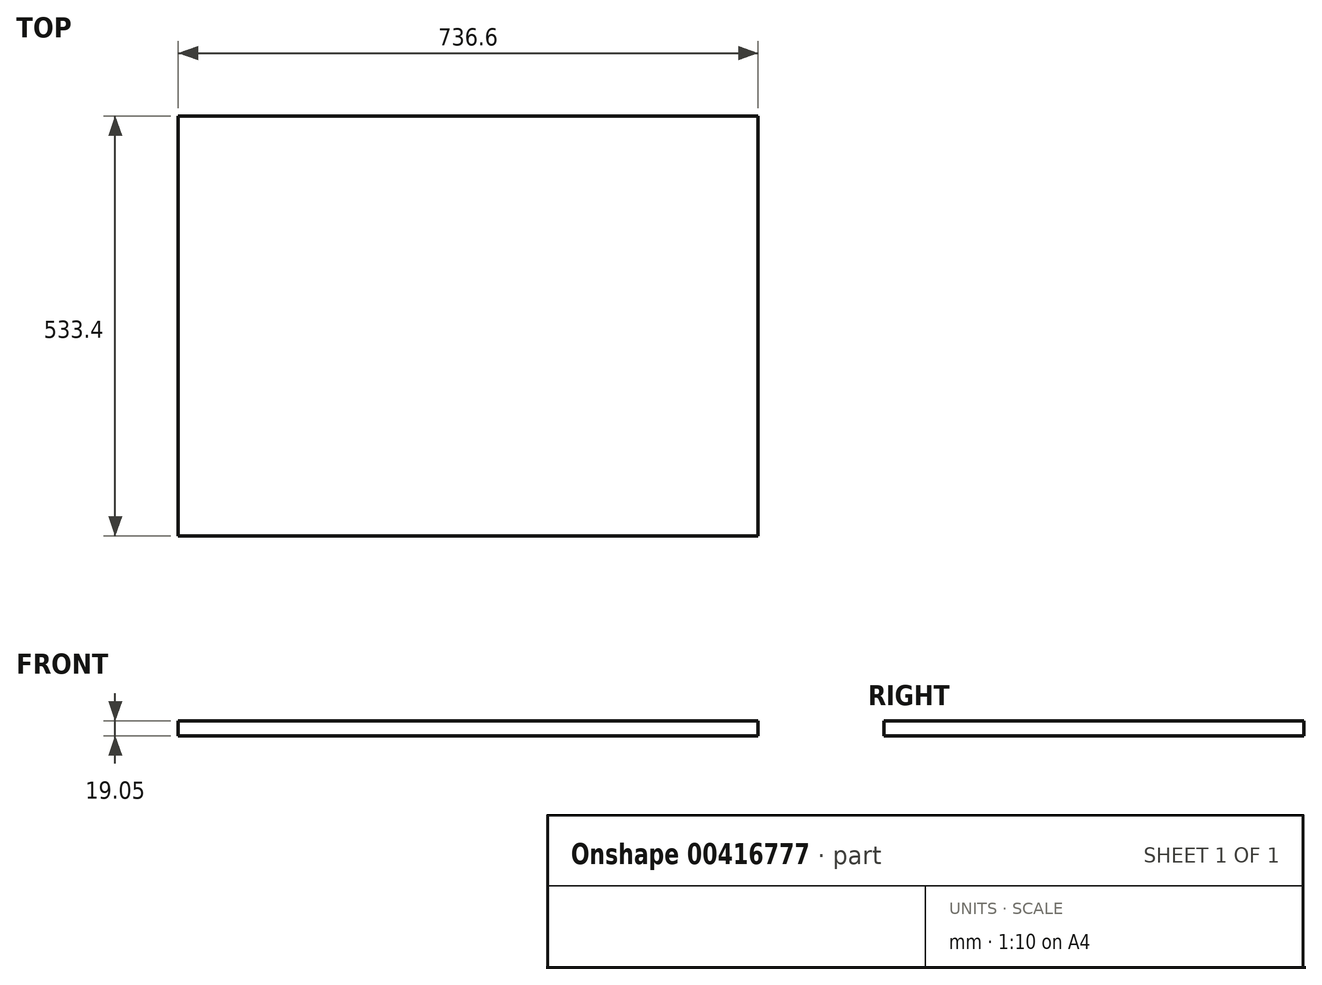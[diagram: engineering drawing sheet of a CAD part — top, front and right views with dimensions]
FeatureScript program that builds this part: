
annotation { "Feature Type Name" : "Feature", "Feature Type Description" : "" }
export const myFeature = defineFeature(function(context is Context, id is Id, definition is map)
    precondition{}
    {
        {
            var Q0;
            Q0=qCreatedBy(makeId("Top.planeOp"),FACE);
            var sketch = newSketch(context, id + "F0", { "sketchPlane" : qUnion([Q0])});
            skLineSegment(sketch, "E0.bottom", {"start": v(0, 0) * mm, "end": v(736.6, 0) * mm});
            skLineSegment(sketch, "E0.top", {"start": v(0, 533.4) * mm, "end": v(736.6, 533.4) * mm});
            skLineSegment(sketch, "E0.left", {"start": v(0, 0) * mm, "end": v(0, 533.4) * mm});
            skLineSegment(sketch, "E0.right", {"start": v(736.6, 0) * mm, "end": v(736.6, 533.4) * mm});
            skSolve(sketch);
        }
        {
            var Q0;
            Q0=makeQuery(id+"F0.imprint","IMPRINT",FACE,{"disambiguationData":[TD([[makeQuery(id+"F0.imprint","IMPRINT",EDGE,{"derivedFrom":sQuery(id+"F0.wireOp",EDGE,"E0.bottom")}),1.0]])]});
            extrude(context, id + "F1", {"entities" : qUnion([Q0]), "depth" : 19.05 * mm});
        }
    });
